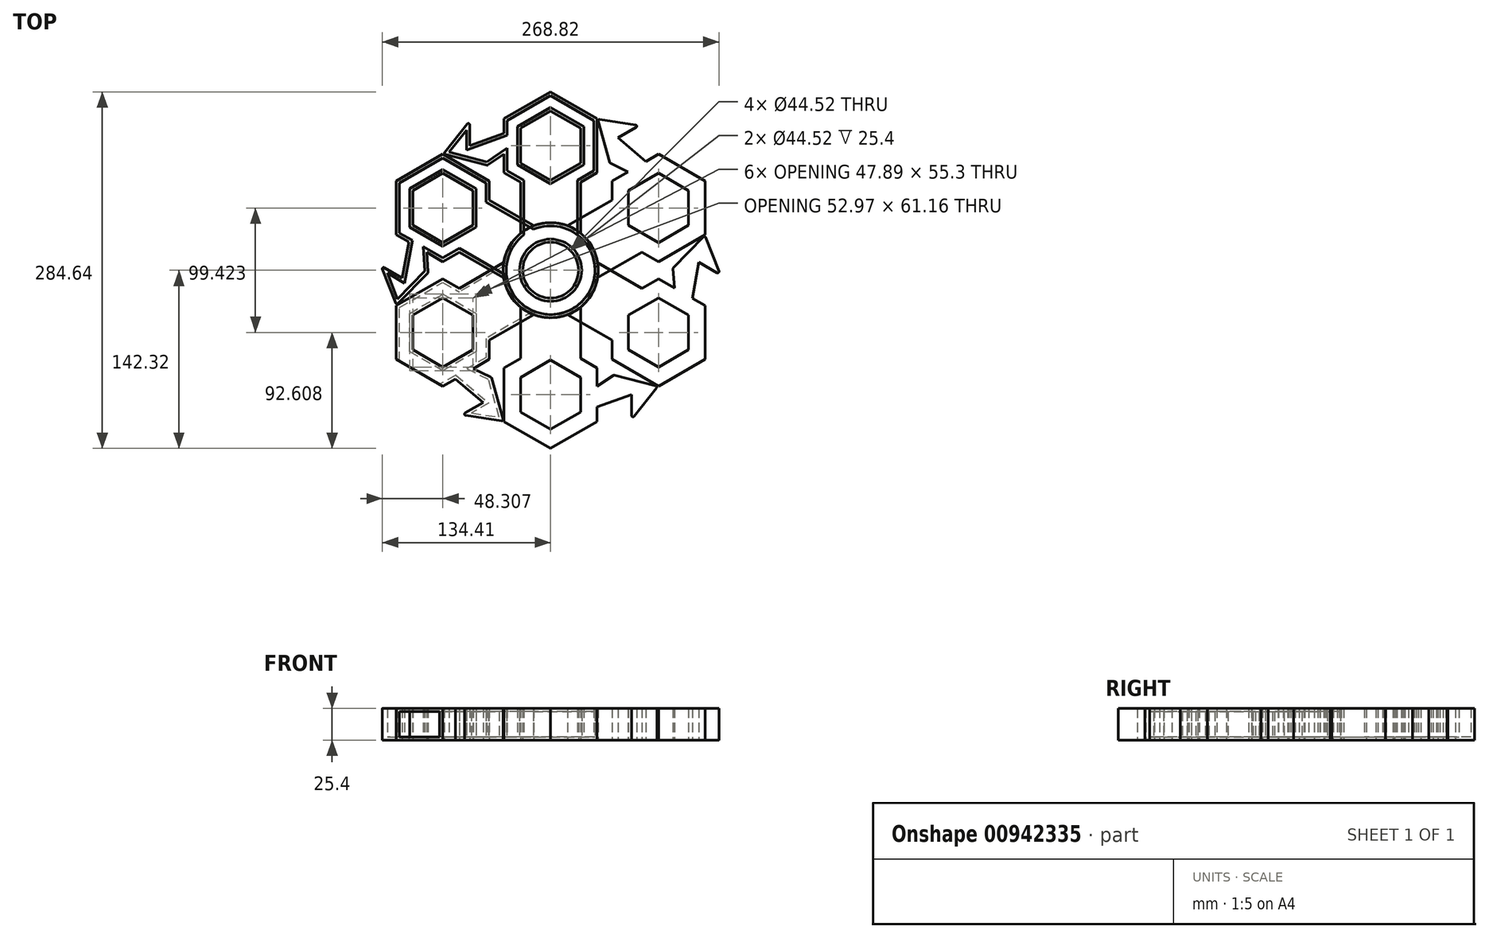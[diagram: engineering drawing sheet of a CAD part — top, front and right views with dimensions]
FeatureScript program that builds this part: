
annotation { "Feature Type Name" : "Feature", "Feature Type Description" : "" }
export const myFeature = defineFeature(function(context is Context, id is Id, definition is map)
    precondition{}
    {
        {
            var Q0;
            Q0=qCreatedBy(makeId("Top.planeOp"),FACE);
            var sketch = newSketch(context, id + "F0", { "sketchPlane" : qUnion([Q0])});
            skCircle(sketch, "E0", {"center": v(0, 0) * mm, "radius": 22.26 * mm});
            skCircle(sketch, "E1", {"center": v(0, 0) * mm, "radius": 37.94 * mm});
            skLineSegment(sketch, "E2", {"start": v(0, 0) * mm, "end": v(0, 93.5) * mm});
            skLineSegment(sketch, "E3", {"start": v(23.94, 29.43) * mm, "end": v(23.94, 85.6) * mm});
            skCircle(sketch, "E4.cCircle", {"center": v(0, 99.42) * mm, "radius": 23.94 * mm, "construction": true});
            skLineSegment(sketch, "E4.0", {"start": v(0, 127.07) * mm, "end": v(23.94, 113.25) * mm});
            skLineSegment(sketch, "E4.1", {"start": v(23.94, 113.25) * mm, "end": v(23.94, 85.6) * mm});
            skLineSegment(sketch, "E4.2", {"start": v(23.94, 85.6) * mm, "end": v(0, 71.77) * mm});
            skLineSegment(sketch, "E4.3", {"start": v(0, 71.77) * mm, "end": v(-23.94, 85.6) * mm});
            skLineSegment(sketch, "E4.4", {"start": v(-23.94, 85.6) * mm, "end": v(-23.94, 113.25) * mm});
            skLineSegment(sketch, "E4.5", {"start": v(-23.94, 113.25) * mm, "end": v(0, 127.07) * mm});
            skPoint(sketch, "E4.0.midPoint", {"position": v(11.97, 120.16) * mm});
            skLineSegment(sketch, "E5.1.0", {"start": v(-86.1, 22.06) * mm, "end": v(-110.05, 35.89) * mm});
            skLineSegment(sketch, "E5.1.1", {"start": v(-110.05, 35.89) * mm, "end": v(-110.05, 63.54) * mm});
            skLineSegment(sketch, "E5.1.2", {"start": v(-110.05, 63.54) * mm, "end": v(-86.1, 77.36) * mm});
            skLineSegment(sketch, "E5.1.3", {"start": v(-86.1, 77.36) * mm, "end": v(-62.16, 63.54) * mm});
            skLineSegment(sketch, "E5.1.4", {"start": v(-62.16, 63.54) * mm, "end": v(-62.16, 35.89) * mm});
            skLineSegment(sketch, "E5.1.5", {"start": v(-62.16, 35.89) * mm, "end": v(-86.1, 22.06) * mm});
            skLineSegment(sketch, "E5.2.0", {"start": v(-62.16, -63.54) * mm, "end": v(-86.1, -77.36) * mm});
            skLineSegment(sketch, "E5.2.1", {"start": v(-86.1, -77.36) * mm, "end": v(-110.05, -63.54) * mm});
            skLineSegment(sketch, "E5.2.2", {"start": v(-110.05, -63.54) * mm, "end": v(-110.05, -35.89) * mm});
            skLineSegment(sketch, "E5.2.3", {"start": v(-110.05, -35.89) * mm, "end": v(-86.1, -22.06) * mm});
            skLineSegment(sketch, "E5.2.4", {"start": v(-86.1, -22.06) * mm, "end": v(-62.16, -35.89) * mm});
            skLineSegment(sketch, "E5.2.5", {"start": v(-62.16, -35.89) * mm, "end": v(-62.16, -63.54) * mm});
            skLineSegment(sketch, "E5.3.0", {"start": v(23.94, -85.6) * mm, "end": v(23.94, -113.25) * mm});
            skLineSegment(sketch, "E5.3.1", {"start": v(23.94, -113.25) * mm, "end": v(0, -127.07) * mm});
            skLineSegment(sketch, "E5.3.2", {"start": v(0, -127.07) * mm, "end": v(-23.94, -113.25) * mm});
            skLineSegment(sketch, "E5.3.3", {"start": v(-23.94, -113.25) * mm, "end": v(-23.94, -85.6) * mm});
            skLineSegment(sketch, "E5.3.4", {"start": v(-23.94, -85.6) * mm, "end": v(0, -71.77) * mm});
            skLineSegment(sketch, "E5.3.5", {"start": v(0, -71.77) * mm, "end": v(23.94, -85.6) * mm});
            skLineSegment(sketch, "E5.4.0", {"start": v(86.1, -22.06) * mm, "end": v(110.05, -35.89) * mm});
            skLineSegment(sketch, "E5.4.1", {"start": v(110.05, -35.89) * mm, "end": v(110.05, -63.54) * mm});
            skLineSegment(sketch, "E5.4.2", {"start": v(110.05, -63.54) * mm, "end": v(86.1, -77.36) * mm});
            skLineSegment(sketch, "E5.4.3", {"start": v(86.1, -77.36) * mm, "end": v(62.16, -63.54) * mm});
            skLineSegment(sketch, "E5.4.4", {"start": v(62.16, -63.54) * mm, "end": v(62.16, -35.89) * mm});
            skLineSegment(sketch, "E5.4.5", {"start": v(62.16, -35.89) * mm, "end": v(86.1, -22.06) * mm});
            skLineSegment(sketch, "E5.5.0", {"start": v(62.16, 63.54) * mm, "end": v(86.1, 77.36) * mm});
            skLineSegment(sketch, "E5.5.1", {"start": v(86.1, 77.36) * mm, "end": v(110.05, 63.54) * mm});
            skLineSegment(sketch, "E5.5.2", {"start": v(110.05, 63.54) * mm, "end": v(110.05, 35.89) * mm});
            skLineSegment(sketch, "E5.5.3", {"start": v(110.05, 35.89) * mm, "end": v(86.1, 22.06) * mm});
            skLineSegment(sketch, "E5.5.4", {"start": v(86.1, 22.06) * mm, "end": v(62.16, 35.89) * mm});
            skLineSegment(sketch, "E5.5.5", {"start": v(62.16, 35.89) * mm, "end": v(62.16, 63.54) * mm});
            skLineSegment(sketch, "E6.MirrorCS", {"start": v(-23.94, 29.43) * mm, "end": v(-23.94, 85.6) * mm});
            skLineSegment(sketch, "E7.0", {"start": v(-37.15, 77.97) * mm, "end": v(-37.15, 120.87) * mm});
            skLineSegment(sketch, "E7.1", {"start": v(0, 142.32) * mm, "end": v(37.15, 120.87) * mm});
            skLineSegment(sketch, "E7.2", {"start": v(37.15, 120.87) * mm, "end": v(37.15, 77.97) * mm});
            skLineSegment(sketch, "E7.3", {"start": v(-37.15, 120.87) * mm, "end": v(0, 142.32) * mm});
            skLineSegment(sketch, "E7.4", {"start": v(37.15, 77.97) * mm, "end": v(0, 56.52) * mm});
            skLineSegment(sketch, "E7.5", {"start": v(0, 56.52) * mm, "end": v(-37.15, 77.97) * mm});
            skLineSegment(sketch, "E8", {"start": v(-37.15, 109.33) * mm, "end": v(-64.66, 99.42) * mm});
            skPoint(sketch, "E8.endSnap0", {"position": v(-37.15, 99.42) * mm});
            skLineSegment(sketch, "E9", {"start": v(-64.66, 99.42) * mm, "end": v(-64.66, 116.14) * mm});
            skLineSegment(sketch, "E10", {"start": v(-66.44, 116.77) * mm, "end": v(-84.62, 94.06) * mm});
            skLineSegment(sketch, "E11", {"start": v(-84.1, 92.46) * mm, "end": v(-50.8, 83.92) * mm});
            skLineSegment(sketch, "E12", {"start": v(-49.98, 84.06) * mm, "end": v(-37.15, 92.74) * mm});
            skPoint(sketch, "E13.visualSharp", {"position": v(-50.36, 83.8) * mm});
            skArc(sketch, "E13.filletArc", {"start": v(-50.8, 83.92) * mm, "mid": v(-50.37, 83.9) * mm, "end": v(-49.98, 84.06) * mm});
            skPoint(sketch, "E14.visualSharp", {"position": v(-85.6, 92.85) * mm});
            skArc(sketch, "E14.filletArc", {"start": v(-84.62, 94.06) * mm, "mid": v(-84.8, 93.11) * mm, "end": v(-84.1, 92.46) * mm});
            skPoint(sketch, "E15.visualSharp", {"position": v(-64.66, 119) * mm});
            skArc(sketch, "E15.filletArc", {"start": v(-64.66, 116.14) * mm, "mid": v(-65.32, 117.09) * mm, "end": v(-66.44, 116.77) * mm});
            skSolve(sketch);
        }
        {
            var Q0;
            Q0=makeQuery(id+"F0.imprint","IMPRINT",FACE,{"disambiguationData":[TD([[makeQuery(id+"F0.imprint","IMPRINT",EDGE,{"derivedFrom":sQuery(id+"F0.wireOp",EDGE,"E4.0")}),1.0]])]});
            var Q1;
            {var subQ0=sQuery(id+"F0.wireOp",EDGE,"E4.3");Q1=makeQuery(id+"F0.imprint","IMPRINT",FACE,{"disambiguationData":[TD([[makeQuery(id+"F0.imprint","IMPRINT",EDGE,{"derivedFrom":subQ0}),1.0]])]});}
            var Q2;
            {var subQ0=sQuery(id+"F0.wireOp",EDGE,"E4.2");Q2=makeQuery(id+"F0.imprint","IMPRINT",FACE,{"disambiguationData":[TD([[makeQuery(id+"F0.imprint","IMPRINT",EDGE,{"derivedFrom":subQ0}),1.0]])]});}
            var Q3;
            {var subQ0=sQuery(id+"F0.wireOp",EDGE,"E3");var subQ1=sQuery(id+"F0.wireOp",EDGE,"E1");var subQ2=makeQuery(id+"F0.imprint","INTERSECT",VERTEX,{"derivedFrom":[subQ1,subQ0]});Q3=makeQuery(id+"F0.imprint","IMPRINT",FACE,{"disambiguationData":[TD([[makeQuery(id+"F0.imprint","IMPRINT",EDGE,{"disambiguationData":[TD([[subQ2,-1.0]])],"derivedFrom":subQ1}),-1.0]])]});}
            var Q4;
            {var subQ0=sQuery(id+"F0.wireOp",EDGE,"E6.MirrorCS");var subQ1=sQuery(id+"F0.wireOp",EDGE,"E1");var subQ2=makeQuery(id+"F0.imprint","INTERSECT",VERTEX,{"derivedFrom":[subQ1,subQ0]});Q4=makeQuery(id+"F0.imprint","IMPRINT",FACE,{"disambiguationData":[TD([[makeQuery(id+"F0.imprint","IMPRINT",EDGE,{"disambiguationData":[TD([[subQ2,1.0]])],"derivedFrom":subQ1}),-1.0]])]});}
            var Q5;
            Q5=makeQuery(id+"F0.imprint","IMPRINT",FACE,{"disambiguationData":[TD([[makeQuery(id+"F0.imprint","IMPRINT",EDGE,{"derivedFrom":sQuery(id+"F0.wireOp",EDGE,"E0")}),-1.0]])]});
            var Q6;
            {var subQ0=sQuery(id+"F0.wireOp",EDGE,"E8");Q6=makeQuery(id+"F0.imprint","IMPRINT",FACE,{"disambiguationData":[TD([[makeQuery(id+"F0.imprint","IMPRINT",EDGE,{"derivedFrom":subQ0}),1.0]])]});}
            var Q7;
            Q7=makeQuery(id+"F0.imprint","IMPRINT",FACE,{"disambiguationData":[TD([[makeQuery(id+"F0.imprint","IMPRINT",EDGE,{"derivedFrom":sQuery(id+"F0.wireOp",EDGE,"E5.1.0")}),-1.0]])]});
            extrude(context, id + "F1", {"entities" : qUnion([Q0, Q1, Q2, Q3, Q4, Q5, Q6, Q7]), "depth" : 25.4 * mm, "offsetDistance" : 25.4 * mm});
        }
        {
            var Q0;
            Q0=qCreatedBy(makeId("Right.planeOp"),FACE);
            var sketch = newSketch(context, id + "F2", { "sketchPlane" : qUnion([Q0])});
            skLineSegment(sketch, "E16", {"start": v(0, 0) * mm, "end": v(0, 59.92) * mm});
            skSolve(sketch);
        }
        {
            var Q0;
            Q0=makeQuery(id+"F1.opExtrude","SWEPT_BODY",BODY,{"disambiguationData":[OSD([sQuery(id+"F0.wireOp",EDGE,"E0"),sQuery(id+"F0.wireOp",EDGE,"E1"),sQuery(id+"F0.wireOp",EDGE,"E3"),sQuery(id+"F0.wireOp",EDGE,"E4.0"),sQuery(id+"F0.wireOp",EDGE,"E4.1"),sQuery(id+"F0.wireOp",EDGE,"E4.2"),sQuery(id+"F0.wireOp",EDGE,"E4.3"),sQuery(id+"F0.wireOp",EDGE,"E4.4"),sQuery(id+"F0.wireOp",EDGE,"E4.5"),sQuery(id+"F0.wireOp",EDGE,"E6.MirrorCS"),sQuery(id+"F0.wireOp",EDGE,"E7.0"),sQuery(id+"F0.wireOp",EDGE,"E7.1"),sQuery(id+"F0.wireOp",EDGE,"E7.2"),sQuery(id+"F0.wireOp",EDGE,"E7.3"),sQuery(id+"F0.wireOp",EDGE,"E7.4"),sQuery(id+"F0.wireOp",EDGE,"E7.5")])]});
            var Q1;
            Q1=sQuery(id+"F2.wireOp",EDGE,"E16");
            circularPattern(context, id + "F3", {"entities" : qUnion([Q0]), "axis" : qUnion([Q1]), "angle" : 360 * degree, "instanceCount" : 6, "equalSpace" : true});
        }
        {
            var Q0;
            Q0=makeQuery(id+"F3.opPattern","COPY",FACE,{"derivedFrom":makeQuery(id+"F1.opExtrude","CAP_FACE",FACE,{"disambiguationData":[OSD([sQuery(id+"F0.wireOp",EDGE,"E0"),sQuery(id+"F0.wireOp",EDGE,"E1"),sQuery(id+"F0.wireOp",EDGE,"E3"),sQuery(id+"F0.wireOp",EDGE,"E4.0"),sQuery(id+"F0.wireOp",EDGE,"E4.1"),sQuery(id+"F0.wireOp",EDGE,"E4.2"),sQuery(id+"F0.wireOp",EDGE,"E4.3"),sQuery(id+"F0.wireOp",EDGE,"E4.4"),sQuery(id+"F0.wireOp",EDGE,"E4.5"),sQuery(id+"F0.wireOp",EDGE,"E6.MirrorCS"),sQuery(id+"F0.wireOp",EDGE,"E7.0"),sQuery(id+"F0.wireOp",EDGE,"E7.1"),sQuery(id+"F0.wireOp",EDGE,"E7.2"),sQuery(id+"F0.wireOp",EDGE,"E7.3"),sQuery(id+"F0.wireOp",EDGE,"E7.4"),sQuery(id+"F0.wireOp",EDGE,"E7.5"),sQuery(id+"F0.wireOp",EDGE,"E8"),sQuery(id+"F0.wireOp",EDGE,"E9"),sQuery(id+"F0.wireOp",EDGE,"E10"),sQuery(id+"F0.wireOp",EDGE,"E11"),sQuery(id+"F0.wireOp",EDGE,"E12")])],"isStart":false}),"instanceName":"1"});
            shell(context, id + "F4", {"entities" : qUnion([Q0]), "thickness" : 2.54 * mm});
        }
        {
            var Q0;
            Q0=makeQuery(id+"F1.opExtrude","CAP_FACE",FACE,{"disambiguationData":[OSD([sQuery(id+"F0.wireOp",EDGE,"E0"),sQuery(id+"F0.wireOp",EDGE,"E1"),sQuery(id+"F0.wireOp",EDGE,"E3"),sQuery(id+"F0.wireOp",EDGE,"E4.0"),sQuery(id+"F0.wireOp",EDGE,"E4.1"),sQuery(id+"F0.wireOp",EDGE,"E4.2"),sQuery(id+"F0.wireOp",EDGE,"E4.3"),sQuery(id+"F0.wireOp",EDGE,"E4.4"),sQuery(id+"F0.wireOp",EDGE,"E4.5"),sQuery(id+"F0.wireOp",EDGE,"E6.MirrorCS"),sQuery(id+"F0.wireOp",EDGE,"E7.0"),sQuery(id+"F0.wireOp",EDGE,"E7.1"),sQuery(id+"F0.wireOp",EDGE,"E7.2"),sQuery(id+"F0.wireOp",EDGE,"E7.3"),sQuery(id+"F0.wireOp",EDGE,"E7.4"),sQuery(id+"F0.wireOp",EDGE,"E7.5"),sQuery(id+"F0.wireOp",EDGE,"E8"),sQuery(id+"F0.wireOp",EDGE,"E9"),sQuery(id+"F0.wireOp",EDGE,"E10"),sQuery(id+"F0.wireOp",EDGE,"E11"),sQuery(id+"F0.wireOp",EDGE,"E12"),sQuery(id+"F0.wireOp",EDGE,"E13.filletArc"),sQuery(id+"F0.wireOp",EDGE,"E14.filletArc"),sQuery(id+"F0.wireOp",EDGE,"E15.filletArc")])],"isStart":false});
            shell(context, id + "F5", {"entities" : qUnion([Q0]), "thickness" : 2.54 * mm});
        }
        {
            var Q0;
            Q0=makeQuery(id+"F3.opPattern","COPY",FACE,{"derivedFrom":makeQuery(id+"F1.opExtrude","SWEPT_FACE",FACE,{"disambiguationData":[OSD([sQuery(id+"F0.wireOp",EDGE,"E7.3")])]}),"instanceName":"2"});
            shell(context, id + "F6", {"entities" : qUnion([Q0]), "thickness" : 2.54 * mm});
        }
    });
